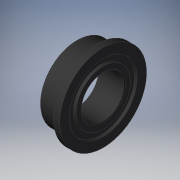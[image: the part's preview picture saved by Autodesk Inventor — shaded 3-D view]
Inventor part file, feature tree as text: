
AUTODESK INVENTOR PART (.ipt)
format: ipt  version: 2019 (Build 230136000, 136)  size: 192,512 bytes
history: native  units: mm
features: other x7, revolve x1, sketch x1
ambient origin geometry x8: Origin, YZ Plane, XZ Plane, XY Plane, X Axis, Y Axis, Z Axis, Center Point
bodies: Solid1 (feature_tree)
feature tree (9):
  revolve  "Revolution1"  [1 undecoded]
  other  "to_housing_XY"
  other  "to_housing_YZ"
  other  "to_housing_ZX"
  other  "to_housing_X"
  other  "to_housing_Y"
  other  "to_housing_Z"
  other  "to_housing_Center"
  sketch  "Sketch_1"  dims[d0=360.0deg d1=0.0mm]
note: 1 required parameter value undecoded (feature->parameter linkage not recoverable at this tier; creation-order binding heuristic only, values carry confidence <= 0.55)
